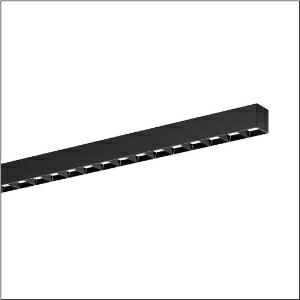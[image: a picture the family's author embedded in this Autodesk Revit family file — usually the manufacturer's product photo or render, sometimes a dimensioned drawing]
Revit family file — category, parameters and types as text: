
# Revit family: silica_r__21_51mx21tat4b_6284
name_source: partatom
category: Lighting Fixtures
units: mm (PartAtom-declared; Revit-internal decimal feet)

## family parameters
Cut with Voids When Loaded = No
Host = Face
Light Source = No
Part Type = Normal
Room Calculation Point = No
Round Connector Dimension = Use Diameter
Shared = No

## types (1)
- --- (1 x LED, 3720 lm, 32.2 W, 6500K)
    Apparent Load = 32 VA
    CIE Flux Codes = 85 99 100 100 100
    Color Rendering = 80
    Color Temperature = 6500K
    Default Elevation = 1800 mm
    Description = Silica® 21, office luminaire, primary light control with darklight reflector, of PMMA, black, CAT 2 (L<= 3000cd/m²), light emission: direct distribution, primary light characteristic: symmetric, installation type: surface-mounted, LED, rated luminous flux: 3.720lm, luminous efficacy: 110lm/W, light colour: 8tw, colour temperature: 2700..6500K, control gear: ECG DALI, with terminal, 3+2-pole, max. 2.5mm², mains connection: 220..240V, AC, 50/60Hz, rated input power: 33.8W, luminaire housing, of aluminium, jet black (RAL 9005), length: 1.204mm, width: 53mm, height: 53mm, protection rating (complete): IP20, insulation class (complete): insulation class I (protective earthing), certification: CE, permissible operating ambient temperature: 0..+35°C, standard: EN 50419, packaging unit: 1 piece
    Height = 0 mm  [stored 0 ft]
    Lamp = 1 x LED
    Lamp Light Flux = 3720 lm
    Lamp Power = 32.2 W
    Lamp count = 1
    Length = 1204 mm
    Luminous efficacy = 116 lm/W
    Manufacturer = Siteco
    ModVariant = No
    Model = 51MX21TAT4B
    Mounting Place = Ceiling
    Mounting Type = Recessed
    Number of Poles = 1
    OnlyDefault = Yes
    Power Factor = 1
    Product Name = Silica® 21
    Product group = office luminaire | ceiling recessed
    ProductGroupID = 401
    Protection Class = Protection class I
    Protection Degree = IP 20
    RLX_Detail_Level = 1
    RLX_Emergency_Light_Flux = 0 lm
    RLX_Emergency_Type = 0
    RLX_Emergency_Type_DB = No
    RlxData = <blob elided: 40213 chars, md5=58865515>
    Socket = socket
    Standby Power = 0 W
    System Light Flux = 3720 lm
    System Power = 32 W
    Type Comments = individual setting
    Type Image = l_1297756.jpg
    URL = http://relux.com
    VarID = @adj_071395
    Voltage = 0 V
    Weight = 0.00 kg
    Width = 53 mm

note: [stored X ft] marks values corroborated as IEEE doubles in the binary element streams (Revit-internal decimal feet)

## geometry (parser evidence)
native form markers: Blend x4, Sweep x9
no freeform markers — native parametric forms only
